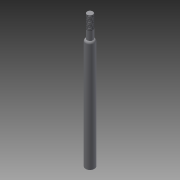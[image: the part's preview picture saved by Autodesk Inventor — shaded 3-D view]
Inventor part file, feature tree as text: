
AUTODESK INVENTOR PART (.ipt)
format: ipt  version: 2015 (Build 190159000, 159)  size: 99,328 bytes
history: native  units: mm
features: extrude x2, fillet x2, sketch x2, thread x1, chamfer x1
ambient origin geometry x8: Origin, YZ Plane, XZ Plane, XY Plane, X Axis, Y Axis, Z Axis, Center Point
bodies: Solid1 (feature_tree)
feature tree (8):
  extrude  "Extrusion1"  Depth=90.0mm TaperAngle=0.0deg
  extrude  "Extrusion2"  Depth=2.0mm TaperAngle=0.0deg
  thread  "Thread1"  [1 undecoded]
  fillet  "Fillet1"  Radius=0.25mm
  fillet  "Fillet2"  Radius=1.5mm
  chamfer  "Chamfer1"  Distance=2.0mm Angle=45.0deg
  sketch  "Sketch1"  dims[d0=6.0mm d1=90.0mm d2=0.0mm]
  sketch  "Sketch2"  dims[d3=4.0mm d4=15.0mm d5=0.0mm d6=10.0mm d7=6.0mm d8=0.25mm d9=1.5mm d10=0.5mm d11=2.0mm d12=45.0deg]
note: 1 required parameter value undecoded (feature->parameter linkage not recoverable at this tier; creation-order binding heuristic only, values carry confidence <= 0.55)
